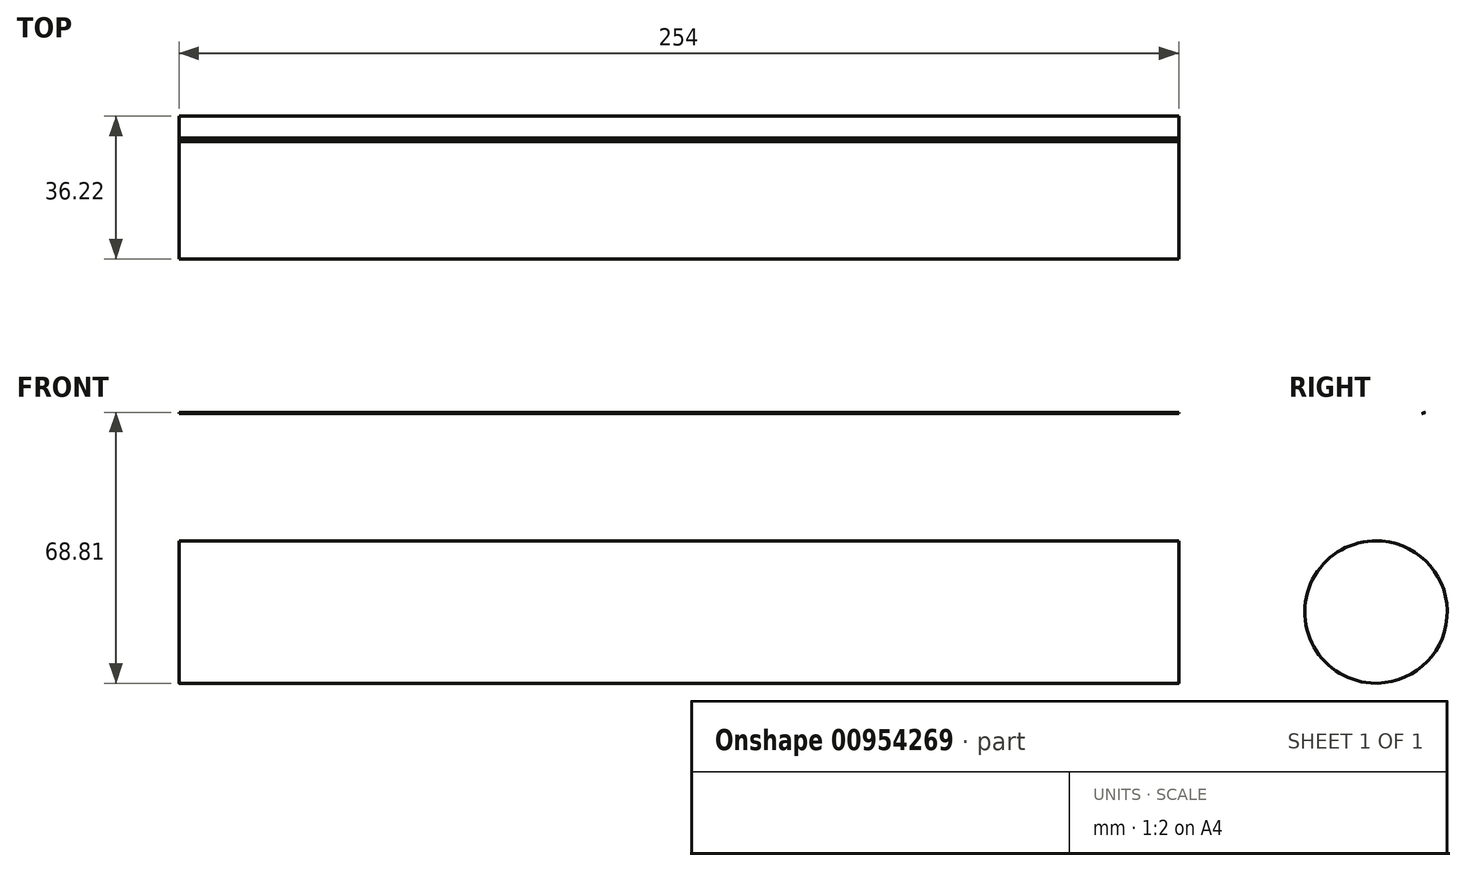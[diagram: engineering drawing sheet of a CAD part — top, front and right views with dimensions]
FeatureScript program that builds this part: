
annotation { "Feature Type Name" : "Feature", "Feature Type Description" : "" }
export const myFeature = defineFeature(function(context is Context, id is Id, definition is map)
    precondition{}
    {
        {
            var Q0;
            Q0=qCreatedBy(makeId("Right.planeOp"),FACE);
            var sketch = newSketch(context, id + "F0", { "sketchPlane" : qUnion([Q0])});
            skArc(sketch, "E0", {"start": v(45.65, 30.43) * mm, "mid": v(65.04, 47.04) * mm, "end": v(48.5, 66.49) * mm});
            skArc(sketch, "E1", {"start": v(48.5, 66.49) * mm, "mid": v(28.94, 49.9) * mm, "end": v(45.65, 30.43) * mm});
            skArc(sketch, "E2", {"start": v(59.56, 99.19) * mm, "mid": v(32.53, 75.37) * mm, "end": v(31.34, 39.37) * mm});
            skArc(sketch, "E3", {"start": v(59.56, 99.19) * mm, "mid": v(57.85, 92.08) * mm, "end": v(64.44, 95.25) * mm});
            skSolve(sketch);
        }
        {
            var Q0;
            {var subQ0=sQuery(id+"F0.wireOp",EDGE,"E3");var subQ1=sQuery(id+"F0.wireOp",EDGE,"E2");var subQ2=makeQuery(id+"F0.imprint","INTERSECT",VERTEX,{"disambiguationData":[OD(0.0)],"derivedFrom":[subQ1,subQ0]});Q0=makeQuery(id+"F0.imprint","IMPRINT",FACE,{"disambiguationData":[TD([[makeQuery(id+"F0.imprint","IMPRINT",EDGE,{"disambiguationData":[TD([[subQ2,-1.0]])],"derivedFrom":subQ1}),-1.0]])]});}
            var Q1;
            {var subQ0=sQuery(id+"F0.wireOp",EDGE,"E2");var subQ1=sQuery(id+"F0.wireOp",EDGE,"E1");var subQ2=makeQuery(id+"F0.imprint","INTERSECT",VERTEX,{"disambiguationData":[OD(0.0)],"derivedFrom":[subQ1,subQ0]});Q1=makeQuery(id+"F0.imprint","IMPRINT",FACE,{"disambiguationData":[TD([[makeQuery(id+"F0.imprint","IMPRINT",EDGE,{"disambiguationData":[TD([[subQ2,1.0]])],"derivedFrom":subQ1}),1.0]])]});}
            var Q2;
            {var subQ0=sQuery(id+"F0.wireOp",EDGE,"E0");Q2=makeQuery(id+"F0.imprint","IMPRINT",FACE,{"disambiguationData":[TD([[makeQuery(id+"F0.imprint","IMPRINT",EDGE,{"derivedFrom":subQ0}),1.0]])]});}
            extrude(context, id + "F1", {"entities" : qUnion([Q0, Q1, Q2]), "depth" : 254 * mm, "offsetDistance" : 25.4 * mm});
        }
    });
